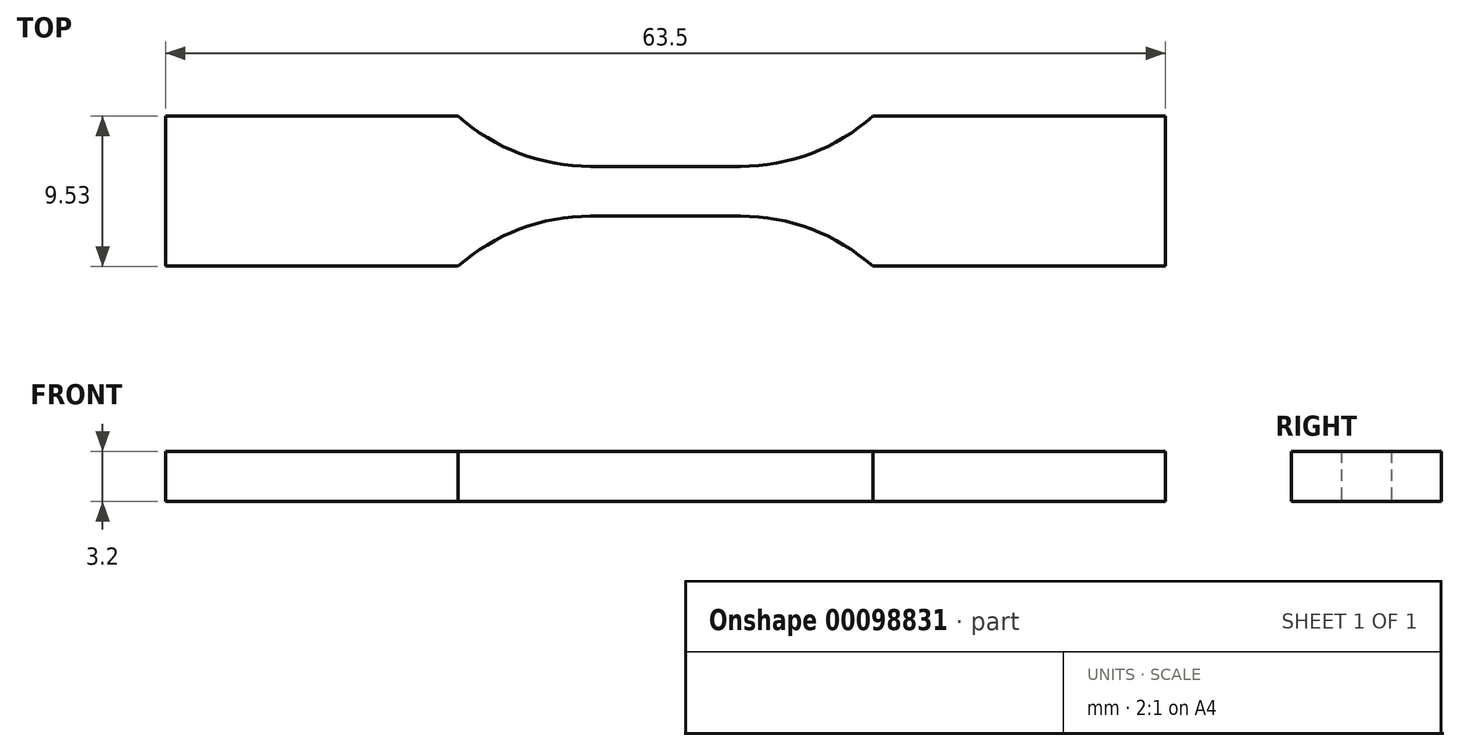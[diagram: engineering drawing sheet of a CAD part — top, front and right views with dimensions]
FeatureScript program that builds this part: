
annotation { "Feature Type Name" : "Feature", "Feature Type Description" : "" }
export const myFeature = defineFeature(function(context is Context, id is Id, definition is map)
    precondition{}
    {
        {
            var Q0;
            Q0=qCreatedBy(makeId("Top.planeOp"),FACE);
            var sketch = newSketch(context, id + "F0", { "sketchPlane" : qUnion([Q0])});
            skLineSegment(sketch, "E0", {"start": v(-18.58, 1.22) * mm, "end": v(0, 1.22) * mm});
            skArc(sketch, "E1", {"start": v(0, 1.22) * mm, "mid": v(3.91, -1.14) * mm, "end": v(8.4, -1.96) * mm});
            skLineSegment(sketch, "E2", {"start": v(8.4, -1.96) * mm, "end": v(13.17, -1.96) * mm});
            skLineSegment(sketch, "E3", {"start": v(-18.58, 1.22) * mm, "end": v(-18.58, -3.54) * mm});
            skLineSegment(sketch, "E4", {"start": v(13.17, -1.96) * mm, "end": v(13.17, -5.14) * mm});
            skLineSegment(sketch, "E5.MirrorCS", {"start": v(17.93, -1.96) * mm, "end": v(13.17, -1.96) * mm});
            skArc(sketch, "E6.MirrorCS", {"start": v(26.34, 1.22) * mm, "mid": v(22.43, -1.14) * mm, "end": v(17.93, -1.96) * mm});
            skLineSegment(sketch, "E7.MirrorCS", {"start": v(44.92, 1.22) * mm, "end": v(44.92, -3.54) * mm});
            skLineSegment(sketch, "E8.MirrorCS", {"start": v(44.92, 1.22) * mm, "end": v(26.34, 1.22) * mm});
            skLineSegment(sketch, "E9", {"start": v(-18.58, -3.54) * mm, "end": v(-12.77, -3.54) * mm});
            skLineSegment(sketch, "E10.MirrorCS", {"start": v(44.92, -8.3) * mm, "end": v(44.92, -3.54) * mm});
            skLineSegment(sketch, "E11.MirrorCS", {"start": v(44.92, -8.3) * mm, "end": v(26.34, -8.3) * mm});
            skArc(sketch, "E12.MirrorCS", {"start": v(26.34, -8.3) * mm, "mid": v(22.43, -5.95) * mm, "end": v(17.93, -5.13) * mm});
            skLineSegment(sketch, "E13.MirrorCS", {"start": v(17.93, -5.13) * mm, "end": v(13.17, -5.13) * mm});
            skLineSegment(sketch, "E14.MirrorCS", {"start": v(8.4, -5.13) * mm, "end": v(13.17, -5.13) * mm});
            skArc(sketch, "E15.MirrorCS", {"start": v(0, -8.3) * mm, "mid": v(3.91, -5.95) * mm, "end": v(8.4, -5.13) * mm});
            skLineSegment(sketch, "E16.MirrorCS", {"start": v(-18.58, -8.3) * mm, "end": v(-18.58, -3.54) * mm});
            skLineSegment(sketch, "E17.MirrorCS", {"start": v(-18.58, -8.3) * mm, "end": v(0, -8.3) * mm});
            skLineSegment(sketch, "E18.MirrorCS", {"start": v(13.17, -5.13) * mm, "end": v(13.17, -1.95) * mm});
            skSolve(sketch);
        }
        {
            var Q0;
            Q0=makeQuery(id+"F0.imprint","IMPRINT",FACE,{"disambiguationData":[TD([[makeQuery(id+"F0.imprint","IMPRINT",EDGE,{"derivedFrom":sQuery(id+"F0.wireOp",EDGE,"E0")}),-1.0]])]});
            var Q1;
            {var subQ1=sQuery(id+"F0.wireOp",EDGE,"E5.MirrorCS");Q1=makeQuery(id+"F0.imprint","IMPRINT",FACE,{"disambiguationData":[TD([[makeQuery(id+"F0.imprint","IMPRINT",EDGE,{"derivedFrom":subQ1}),1.0]])]});}
            var Q2;
            Q2=sQuery(id+"F0.wireOp",EDGE,"E0");
            var Q3;
            Q3=sQuery(id+"F0.wireOp",EDGE,"990227b5-0faf-45ab-b2e8-708ace853b6d");
            var Q4;
            Q4=sQuery(id+"F0.wireOp",EDGE,"E1");
            var Q5;
            Q5=sQuery(id+"F0.wireOp",EDGE,"E2");
            var Q6;
            Q6=sQuery(id+"F0.wireOp",EDGE,"E3");
            var Q7;
            Q7=sQuery(id+"F0.wireOp",EDGE,"E4");
            var Q8;
            Q8=sQuery(id+"F0.wireOp",EDGE,"e609ce1d-7bd1-49a0-b337-821fabe53d26.MirrorCS");
            var Q9;
            Q9=sQuery(id+"F0.wireOp",EDGE,"6d0b48dd-3820-4b0b-a7b8-167a495664b3.MirrorCS");
            var Q10;
            Q10=sQuery(id+"F0.wireOp",EDGE,"fa3660b8-ca54-4300-afb4-eb0de3475f41.MirrorCS");
            var Q11;
            Q11=sQuery(id+"F0.wireOp",EDGE,"e4e8c5f1-0071-40dd-a559-ebd05e820f05.MirrorCS");
            var Q12;
            Q12=sQuery(id+"F0.wireOp",EDGE,"eb095ca0-bb3a-4696-bc5d-a5fc55e6f7e0.MirrorCS");
            var Q13;
            Q13=sQuery(id+"F0.wireOp",EDGE,"cb5a2794-c713-46b6-b01a-2a80fab785a6.MirrorCS");
            var Q14;
            Q14=sQuery(id+"F0.wireOp",EDGE,"95789ff8-829e-4520-8e25-3ff78bb640d5.MirrorCS");
            var Q15;
            Q15=sQuery(id+"F0.wireOp",EDGE,"cef6ef88-108f-4d05-9a11-f4324a5adcce.MirrorCS");
            var Q16;
            Q16=sQuery(id+"F0.wireOp",EDGE,"092fb062-748f-443e-8fca-8fffc5d67888.MirrorCS");
            var Q17;
            Q17=sQuery(id+"F0.wireOp",EDGE,"f09a2a1c-014c-4ab1-83bc-a73d188b7fa8.MirrorCS");
            var Q18;
            Q18=sQuery(id+"F0.wireOp",EDGE,"72719aed-3e7b-49ee-bc84-8557fc4694a1.MirrorCS");
            var Q19;
            Q19=sQuery(id+"F0.wireOp",EDGE,"fcfeace5-cd93-4f81-9bfa-ce2df98311a7.MirrorCS");
            var Q20;
            Q20=sQuery(id+"F0.wireOp",EDGE,"8134f235-6c67-4b23-8965-98fb9846efde.MirrorCS");
            var Q21;
            Q21=sQuery(id+"F0.wireOp",EDGE,"279170bf-8566-43e1-a652-1ce728103c68.MirrorCS");
            var Q22;
            Q22=sQuery(id+"F0.wireOp",EDGE,"71ad9d3b-b57d-4cbe-b739-954955bc877f.MirrorCS");
            extrude(context, id + "F1", {"entities" : qUnion([Q0, Q1]), "surfaceEntities" : qUnion([Q2, Q3, Q4, Q5, Q6, Q7, Q8, Q9, Q10, Q11, Q12, Q13, Q14, Q15, Q16, Q17, Q18, Q19, Q20, Q21, Q22]), "offsetDistance" : 25 * mm, "depth" : 3.2 * mm});
        }
    });
